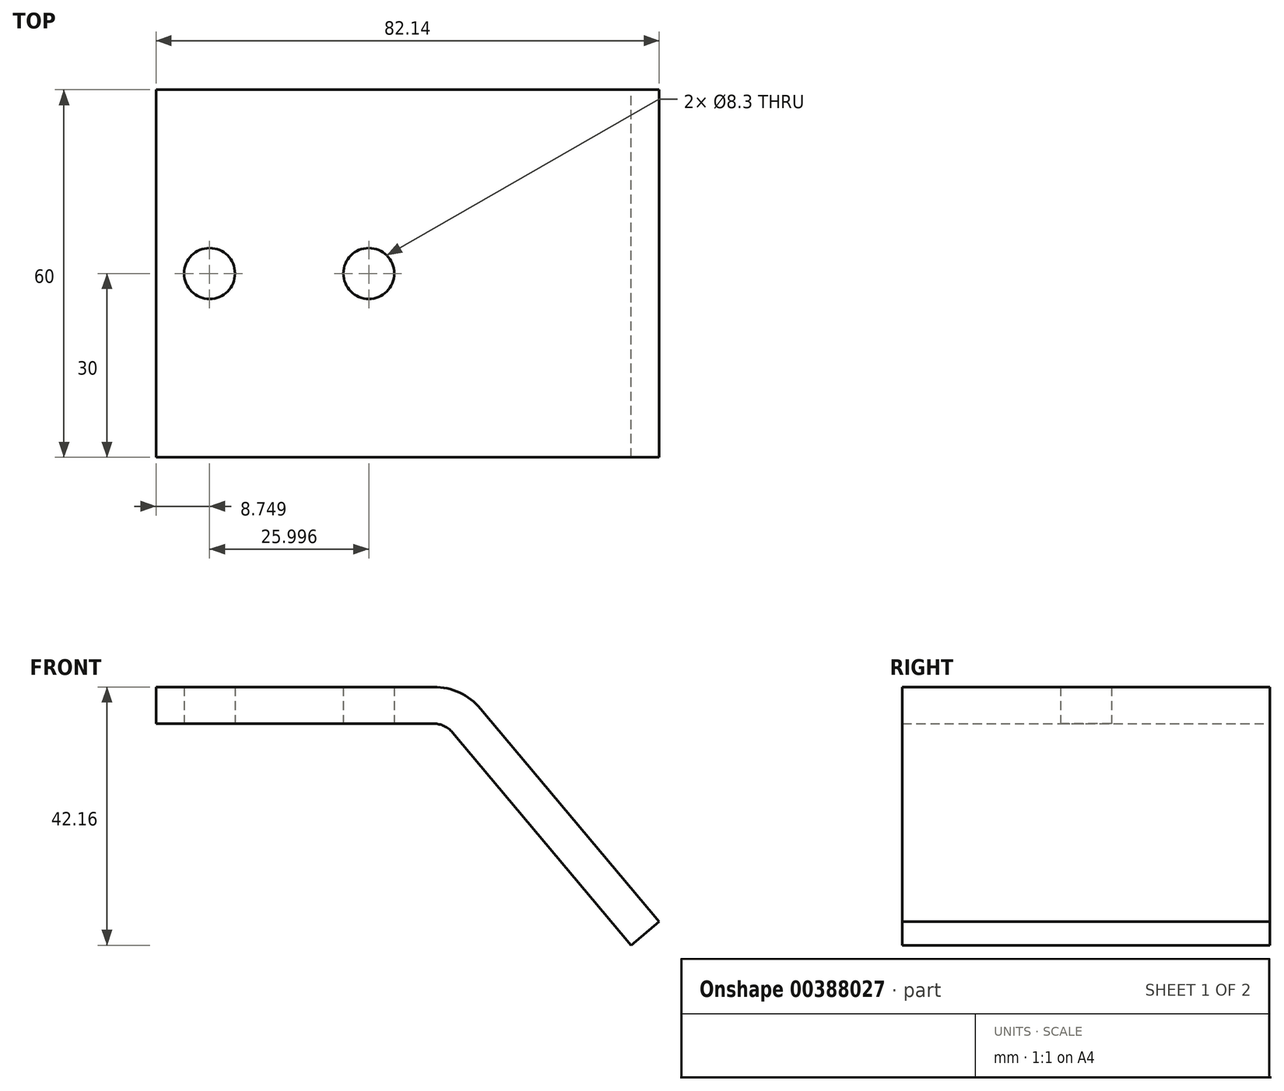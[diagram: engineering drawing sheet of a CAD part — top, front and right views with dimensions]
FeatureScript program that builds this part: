
annotation { "Feature Type Name" : "Feature", "Feature Type Description" : "" }
export const myFeature = defineFeature(function(context is Context, id is Id, definition is map)
    precondition{}
    {
        {
            var Q0;
            Q0=qCreatedBy(makeId("Front.planeOp"),FACE);
            var sketch = newSketch(context, id + "F0", { "sketchPlane" : qUnion([Q0])});
            skLineSegment(sketch, "E0", {"start": v(-50, 32.53) * mm, "end": v(-4.66, 32.53) * mm});
            skLineSegment(sketch, "E1", {"start": v(3, 28.96) * mm, "end": v(32.14, -5.77) * mm});
            skPoint(sketch, "E2.visualSharp", {"position": v(0, 32.53) * mm});
            skArc(sketch, "E2.filletArc", {"start": v(3, 28.96) * mm, "mid": v(-0.44, 31.6) * mm, "end": v(-4.66, 32.53) * mm});
            skLineSegment(sketch, "E3.0", {"start": v(-1.6, 25.1) * mm, "end": v(27.54, -9.63) * mm});
            skArc(sketch, "E3.1", {"start": v(-1.6, 25.1) * mm, "mid": v(-2.97, 26.16) * mm, "end": v(-4.66, 26.53) * mm});
            skLineSegment(sketch, "E3.2", {"start": v(-50, 26.53) * mm, "end": v(-4.66, 26.53) * mm});
            skLineSegment(sketch, "E4", {"start": v(-50, 32.53) * mm, "end": v(-50, 26.53) * mm});
            skLineSegment(sketch, "E5", {"start": v(27.54, -9.63) * mm, "end": v(32.14, -5.77) * mm});
            skSolve(sketch);
        }
        {
            var Q0;
            Q0 = qSketchRegion(id + "F0", true);
            extrude(context, id + "F1", {"entities" : qUnion([Q0]), "depth" : 60 * mm, "offsetDistance" : 25 * mm});
        }
        {
            var Q0;
            Q0=makeQuery(id+"F1.opExtrude","SWEPT_FACE",FACE,{"disambiguationData":[OSD([sQuery(id+"F0.wireOp",EDGE,"E3.2")])]});
            var sketch = newSketch(context, id + "F2", { "sketchPlane" : qUnion([Q0])});
            skLineSegment(sketch, "E6", {"start": v(-50, 30) * mm, "end": v(-4.66, 30) * mm, "construction": true});
            skCircle(sketch, "E7", {"center": v(-41.25, 30) * mm, "radius": 4.15 * mm});
            skCircle(sketch, "E8", {"center": v(-15.26, 30) * mm, "radius": 4.15 * mm});
            skSolve(sketch);
        }
        {
            var Q0;
            Q0 = qSketchRegion(id + "F2", true);
            extrude(context, id + "F3", {"entities" : qUnion([Q0]), "operationType" : NewBodyOperationType.REMOVE, "oppositeDirection" : true, "depth" : 25 * mm, "offsetDistance" : 25 * mm});
        }
    });
